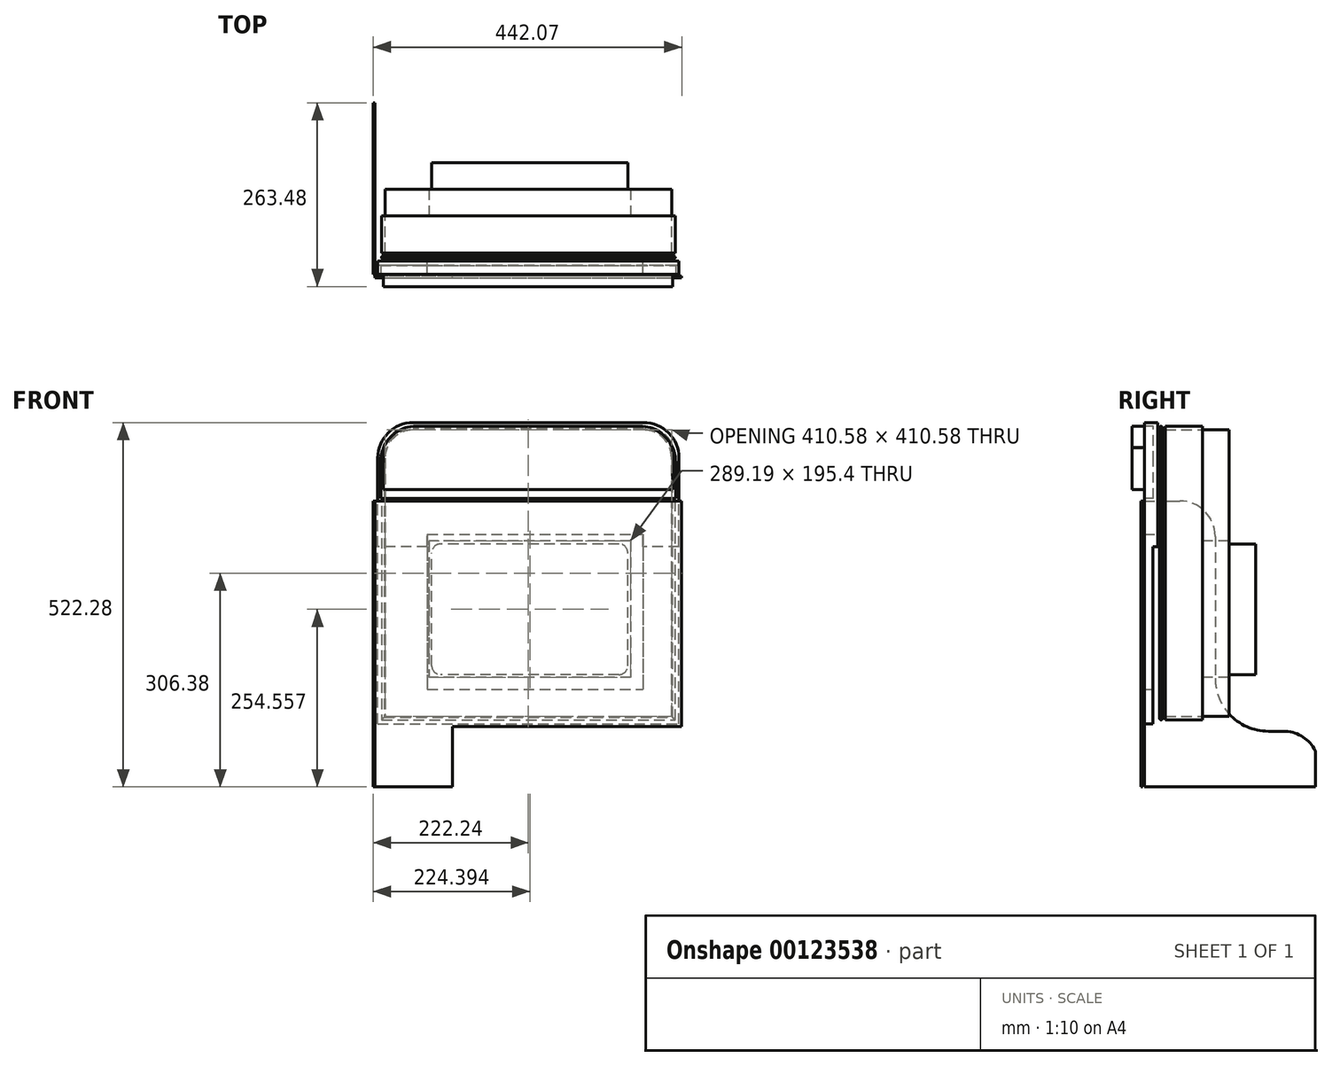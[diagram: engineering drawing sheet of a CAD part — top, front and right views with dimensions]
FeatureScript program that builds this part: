
annotation { "Feature Type Name" : "Feature", "Feature Type Description" : "" }
export const myFeature = defineFeature(function(context is Context, id is Id, definition is map)
    precondition{}
    {
        {
            var Q0;
            Q0=qCreatedBy(makeId("Front.planeOp"),FACE);
            var sketch = newSketch(context, id + "F0", { "sketchPlane" : qUnion([Q0])});
            skLineSegment(sketch, "E0.bottom", {"start": v(0, 0) * mm, "end": v(431.8, 0) * mm});
            skLineSegment(sketch, "E0.top", {"start": v(50.8, 431.8) * mm, "end": v(381, 431.8) * mm});
            skLineSegment(sketch, "E0.left", {"start": v(0, 0) * mm, "end": v(0, 381) * mm});
            skLineSegment(sketch, "E0.right", {"start": v(431.8, 0) * mm, "end": v(431.8, 381) * mm});
            skPoint(sketch, "E1.visualSharp", {"position": v(0, 431.8) * mm});
            skArc(sketch, "E1.filletArc", {"start": v(50.8, 431.8) * mm, "mid": v(14.88, 416.92) * mm, "end": v(0, 381) * mm});
            skPoint(sketch, "E2.visualSharp", {"position": v(431.8, 431.8) * mm});
            skArc(sketch, "E2.filletArc", {"start": v(431.8, 381) * mm, "mid": v(416.92, 416.92) * mm, "end": v(381, 431.8) * mm});
            skSolve(sketch);
        }
        {
            var Q0;
            Q0 = qSketchRegion(id + "F0", true);
            extrude(context, id + "F1", {"entities" : qUnion([Q0]), "depth" : 19.05 * mm});
        }
        {
            var Q0;
            Q0=makeQuery(id+"F1.opExtrude","SWEPT_FACE",FACE,{"disambiguationData":[OSD([sQuery(id+"F0.wireOp",EDGE,"E0.left")])]});
            var sketch = newSketch(context, id + "F2", { "sketchPlane" : qUnion([Q0])});
            skLineSegment(sketch, "E3.bottom", {"start": v(0, 0) * mm, "end": v(6.8, 0) * mm});
            skLineSegment(sketch, "E3.top", {"start": v(0, 254) * mm, "end": v(6.8, 254) * mm});
            skLineSegment(sketch, "E3.left", {"start": v(0, 0) * mm, "end": v(0, 254) * mm});
            skLineSegment(sketch, "E3.right", {"start": v(6.8, 0) * mm, "end": v(6.8, 254) * mm});
            skSolve(sketch);
        }
        {
            var Q0;
            Q0=makeQuery(id+"F2.imprint","IMPRINT",FACE,{"disambiguationData":[TD([[makeQuery(id+"F2.imprint","IMPRINT",EDGE,{"derivedFrom":sQuery(id+"F2.wireOp",EDGE,"E3.bottom")}),-1.0]])]});
            extrude(context, id + "F3", {"entities" : qUnion([Q0]), "operationType" : NewBodyOperationType.REMOVE, "oppositeDirection" : true, "depth" : 431.8 * mm});
        }
        {
            var Q0;
            Q0=makeQuery(id+"F0.imprint","IMPRINT",FACE,{"disambiguationData":[TD([[makeQuery(id+"F0.imprint","IMPRINT",EDGE,{"derivedFrom":sQuery(id+"F0.wireOp",EDGE,"E0.bottom")}),1.0]])]});
            var sketch = newSketch(context, id + "F4", { "sketchPlane" : qUnion([Q0])});
            skLineSegment(sketch, "E4.bottom", {"start": v(380.1, 49.43) * mm, "end": v(71.18, 49.43) * mm});
            skLineSegment(sketch, "E4.top", {"start": v(380.1, 271.62) * mm, "end": v(71.18, 271.62) * mm});
            skLineSegment(sketch, "E4.left", {"start": v(380.1, 49.43) * mm, "end": v(380.1, 271.62) * mm});
            skLineSegment(sketch, "E4.right", {"start": v(71.18, 49.43) * mm, "end": v(71.18, 271.62) * mm});
            skSolve(sketch);
        }
        {
            var Q0;
            Q0 = qSketchRegion(id + "F4", true);
            extrude(context, id + "F5", {"entities" : qUnion([Q0]), "operationType" : NewBodyOperationType.REMOVE, "depth" : 25.4 * mm});
        }
        {
            var Q0;
            Q0=qCreatedBy(makeId("Right.planeOp"),FACE);
            var sketch = newSketch(context, id + "F6", { "sketchPlane" : qUnion([Q0])});
            skCircle(sketch, "E5", {"center": v(4.9, 7.38) * mm, "radius": 1.9 * mm});
            skSolve(sketch);
        }
        {
            var Q0;
            Q0=makeQuery(id+"F6.imprint","IMPRINT",FACE,{"disambiguationData":[TD([[makeQuery(id+"F6.imprint","IMPRINT",EDGE,{"derivedFrom":sQuery(id+"F6.wireOp",EDGE,"E5")}),1.0]])]});
            var Q1;
            Q1=sQuery(id+"F0.wireOp",EDGE,"E0.right");
            var Q2;
            Q2=sQuery(id+"F0.wireOp",EDGE,"E2.filletArc");
            var Q3;
            Q3=sQuery(id+"F0.wireOp",EDGE,"E0.top");
            var Q4;
            Q4=sQuery(id+"F0.wireOp",EDGE,"E1.filletArc");
            var Q5;
            Q5=sQuery(id+"F0.wireOp",EDGE,"E0.left");
            var Q6;
            Q6=sQuery(id+"F0.wireOp",EDGE,"E0.bottom");
            sweep(context, id + "F7", {"profiles" : qUnion([Q0]), "path" : qUnion([Q1, Q2, Q3, Q4, Q5, Q6])});
        }
        {
            var Q0;
            Q0=qCreatedBy(makeId("Right.planeOp"),FACE);
            var sketch = newSketch(context, id + "F8", { "sketchPlane" : qUnion([Q0])});
            skLineSegment(sketch, "E6.bottom", {"start": v(11.24, 5.26) * mm, "end": v(64.2, 5.26) * mm});
            skLineSegment(sketch, "E6.top", {"start": v(11.24, 10.61) * mm, "end": v(64.2, 10.61) * mm});
            skLineSegment(sketch, "E6.left", {"start": v(11.24, 5.26) * mm, "end": v(11.24, 10.61) * mm});
            skLineSegment(sketch, "E6.right", {"start": v(64.2, 5.26) * mm, "end": v(64.2, 10.61) * mm});
            skSolve(sketch);
        }
        {
            var Q0;
            Q0=makeQuery(id+"F8.imprint","IMPRINT",FACE,{"disambiguationData":[TD([[makeQuery(id+"F8.imprint","IMPRINT",EDGE,{"derivedFrom":sQuery(id+"F8.wireOp",EDGE,"E6.bottom")}),1.0]])]});
            var Q1;
            Q1=makeQuery(id+"F1.opExtrude","CAP_EDGE",EDGE,{"disambiguationData":[OSD([sQuery(id+"F0.wireOp",EDGE,"E0.left")])],"isStart":false});
            var Q2;
            Q2=makeQuery(id+"F1.opExtrude","CAP_EDGE",EDGE,{"disambiguationData":[OSD([sQuery(id+"F0.wireOp",EDGE,"E1.filletArc")])],"isStart":false});
            var Q3;
            Q3=makeQuery(id+"F1.opExtrude","CAP_EDGE",EDGE,{"disambiguationData":[OSD([sQuery(id+"F0.wireOp",EDGE,"E0.top")])],"isStart":false});
            var Q4;
            Q4=makeQuery(id+"F1.opExtrude","CAP_EDGE",EDGE,{"disambiguationData":[OSD([sQuery(id+"F0.wireOp",EDGE,"E2.filletArc")])],"isStart":false});
            var Q5;
            Q5=makeQuery(id+"F1.opExtrude","CAP_EDGE",EDGE,{"disambiguationData":[OSD([sQuery(id+"F0.wireOp",EDGE,"E0.right")])],"isStart":false});
            var Q6;
            Q6=makeQuery(id+"F1.opExtrude","CAP_EDGE",EDGE,{"disambiguationData":[OSD([sQuery(id+"F0.wireOp",EDGE,"E0.bottom")])],"isStart":false});
            sweep(context, id + "F9", {"profiles" : qUnion([Q0]), "path" : qUnion([Q1, Q2, Q3, Q4, Q5, Q6])});
        }
        {
            var Q0;
            Q0=makeQuery(id+"F1.opExtrude","CAP_FACE",FACE,{"disambiguationData":[OSD([sQuery(id+"F0.wireOp",EDGE,"E0.bottom"),sQuery(id+"F0.wireOp",EDGE,"E0.top"),sQuery(id+"F0.wireOp",EDGE,"E0.left"),sQuery(id+"F0.wireOp",EDGE,"E0.right"),sQuery(id+"F0.wireOp",EDGE,"E1.filletArc"),sQuery(id+"F0.wireOp",EDGE,"E2.filletArc")])],"isStart":false});
            var sketch = newSketch(context, id + "F10", { "sketchPlane" : qUnion([Q0])});
            skLineSegment(sketch, "E7.bottom", {"start": v(4.2, 322.79) * mm, "end": v(426.84, 322.79) * mm});
            skLineSegment(sketch, "E7.top", {"start": v(55, 426.58) * mm, "end": v(376.04, 426.58) * mm});
            skLineSegment(sketch, "E7.left", {"start": v(4.2, 322.79) * mm, "end": v(4.2, 375.78) * mm});
            skLineSegment(sketch, "E7.right", {"start": v(426.84, 322.79) * mm, "end": v(426.84, 375.78) * mm});
            skPoint(sketch, "E8.visualSharp", {"position": v(4.2, 426.58) * mm});
            skArc(sketch, "E8.filletArc", {"start": v(55, 426.58) * mm, "mid": v(19.07, 411.7) * mm, "end": v(4.2, 375.78) * mm});
            skPoint(sketch, "E9.visualSharp", {"position": v(426.84, 426.58) * mm});
            skArc(sketch, "E9.filletArc", {"start": v(426.84, 375.78) * mm, "mid": v(411.97, 411.7) * mm, "end": v(376.04, 426.58) * mm});
            skSolve(sketch);
        }
        {
            var Q0;
            Q0=makeQuery(id+"F10.imprint","IMPRINT",FACE,{"disambiguationData":[TD([[makeQuery(id+"F10.imprint","IMPRINT",EDGE,{"derivedFrom":sQuery(id+"F10.wireOp",EDGE,"E7.bottom")}),1.0]])]});
            extrude(context, id + "F11", {"entities" : qUnion([Q0]), "operationType" : NewBodyOperationType.REMOVE, "oppositeDirection" : true, "depth" : 12.7 * mm});
        }
        {
            var Q0;
            Q0=makeQuery(id+"F1.opExtrude","CAP_FACE",FACE,{"disambiguationData":[OSD([sQuery(id+"F0.wireOp",EDGE,"E0.bottom"),sQuery(id+"F0.wireOp",EDGE,"E0.top"),sQuery(id+"F0.wireOp",EDGE,"E0.left"),sQuery(id+"F0.wireOp",EDGE,"E0.right"),sQuery(id+"F0.wireOp",EDGE,"E1.filletArc"),sQuery(id+"F0.wireOp",EDGE,"E2.filletArc")])],"isStart":false});
            var sketch = newSketch(context, id + "F12", { "sketchPlane" : qUnion([Q0])});
            skLineSegment(sketch, "E10.bottom", {"start": v(7.94, 335.82) * mm, "end": v(422.56, 335.82) * mm});
            skLineSegment(sketch, "E10.top", {"start": v(58.74, 450.12) * mm, "end": v(371.76, 450.12) * mm});
            skLineSegment(sketch, "E10.left", {"start": v(7.94, 335.82) * mm, "end": v(7.94, 399.32) * mm});
            skLineSegment(sketch, "E10.right", {"start": v(422.56, 335.82) * mm, "end": v(422.56, 399.32) * mm});
            skPoint(sketch, "E11.visualSharp", {"position": v(7.94, 450.12) * mm});
            skArc(sketch, "E11.filletArc", {"start": v(58.74, 450.12) * mm, "mid": v(22.81, 435.24) * mm, "end": v(7.94, 399.32) * mm});
            skPoint(sketch, "E12.visualSharp", {"position": v(422.56, 450.12) * mm});
            skArc(sketch, "E12.filletArc", {"start": v(422.56, 399.32) * mm, "mid": v(407.69, 435.24) * mm, "end": v(371.76, 450.12) * mm});
            skSolve(sketch);
        }
        {
            var Q0;
            {var subQ2=sQuery(id+"F12.wireOp",EDGE,"E10.bottom");Q0=makeQuery(id+"F12.imprint","IMPRINT",FACE,{"disambiguationData":[TD([[makeQuery(id+"F12.imprint","IMPRINT",EDGE,{"derivedFrom":subQ2}),1.0]])]});}
            extrude(context, id + "F13", {"entities" : qUnion([Q0]), "depth" : 17.78 * mm});
        }
        {
            var Q0;
            Q0=makeQuery(id+"F9.opSweep","SWEPT_FACE",FACE,{"disambiguationData":[OSD([sQuery(id+"F0.wireOp",EDGE,"E0.bottom"),sQuery(id+"F8.wireOp",EDGE,"E6.right")])]});
            var sketch = newSketch(context, id + "F14", { "sketchPlane" : qUnion([Q0])});
            skLineSegment(sketch, "E13.bottom", {"start": v(-432.22, 0) * mm, "end": v(0, 0) * mm});
            skLineSegment(sketch, "E13.top", {"start": v(-381.42, 432.66) * mm, "end": v(-50.8, 432.66) * mm});
            skLineSegment(sketch, "E13.left", {"start": v(-432.22, 0) * mm, "end": v(-432.22, 381.86) * mm});
            skLineSegment(sketch, "E13.right", {"start": v(0, 0) * mm, "end": v(0, 381.86) * mm});
            skPoint(sketch, "E14.visualSharp", {"position": v(-432.22, 432.66) * mm});
            skArc(sketch, "E14.filletArc", {"start": v(-425.87, 432.66) * mm, "mid": v(-430.36, 430.8) * mm, "end": v(-432.22, 426.3) * mm});
            skPoint(sketch, "E15.visualSharp", {"position": v(0, 432.66) * mm});
            skArc(sketch, "E15.filletArc", {"start": v(0, 381.86) * mm, "mid": v(-14.88, 417.78) * mm, "end": v(-50.8, 432.66) * mm});
            skArc(sketch, "E16.filletArc", {"start": v(-381.42, 432.66) * mm, "mid": v(-417.34, 417.78) * mm, "end": v(-432.22, 381.86) * mm});
            skLineSegment(sketch, "E17.bottom", {"start": v(-362.65, 261.78) * mm, "end": v(-73.46, 261.78) * mm});
            skLineSegment(sketch, "E17.top", {"start": v(-362.65, 66.38) * mm, "end": v(-73.46, 66.38) * mm});
            skLineSegment(sketch, "E17.left", {"start": v(-362.65, 261.78) * mm, "end": v(-362.65, 66.38) * mm});
            skLineSegment(sketch, "E17.right", {"start": v(-73.46, 261.78) * mm, "end": v(-73.46, 66.38) * mm});
            skSolve(sketch);
        }
        {
            var Q0;
            Q0=makeQuery(id+"F14.imprint","IMPRINT",FACE,{"disambiguationData":[TD([[makeQuery(id+"F14.imprint","IMPRINT",EDGE,{"derivedFrom":sQuery(id+"F14.wireOp",EDGE,"E17.bottom")}),1.0]])]});
            extrude(context, id + "F15", {"entities" : qUnion([Q0]), "depth" : 38.1 * mm});
        }
        {
            var Q0;
            Q0=makeQuery(id+"F15.opExtrude","CAP_FACE",FACE,{"disambiguationData":[OSD([sQuery(id+"F0.wireOp",EDGE,"E0.bottom"),sQuery(id+"F0.wireOp",EDGE,"E0.top"),sQuery(id+"F0.wireOp",EDGE,"E0.left"),sQuery(id+"F0.wireOp",EDGE,"E0.right"),sQuery(id+"F0.wireOp",EDGE,"E1.filletArc"),sQuery(id+"F0.wireOp",EDGE,"E2.filletArc"),sQuery(id+"F8.wireOp",EDGE,"E6.top"),sQuery(id+"F8.wireOp",EDGE,"E6.right"),sQuery(id+"F14.wireOp",EDGE,"E17.bottom"),sQuery(id+"F14.wireOp",EDGE,"E17.top"),sQuery(id+"F14.wireOp",EDGE,"E17.left"),sQuery(id+"F14.wireOp",EDGE,"E17.right")])],"isStart":false});
            var sketch = newSketch(context, id + "F16", { "sketchPlane" : qUnion([Q0])});
            skLineSegment(sketch, "E18.bottom", {"start": v(-345.82, 70.33) * mm, "end": v(-90.05, 70.33) * mm});
            skLineSegment(sketch, "E18.top", {"start": v(-345.82, 257.63) * mm, "end": v(-90.05, 257.63) * mm});
            skLineSegment(sketch, "E18.left", {"start": v(-358.52, 83.03) * mm, "end": v(-358.52, 244.93) * mm});
            skLineSegment(sketch, "E18.right", {"start": v(-77.35, 83.03) * mm, "end": v(-77.35, 244.93) * mm});
            skPoint(sketch, "E19.visualSharp", {"position": v(-358.52, 257.63) * mm});
            skArc(sketch, "E19.filletArc", {"start": v(-345.82, 257.63) * mm, "mid": v(-354.8, 253.91) * mm, "end": v(-358.52, 244.93) * mm});
            skPoint(sketch, "E20.visualSharp", {"position": v(-77.35, 257.63) * mm});
            skArc(sketch, "E20.filletArc", {"start": v(-77.35, 244.93) * mm, "mid": v(-81.07, 253.91) * mm, "end": v(-90.05, 257.63) * mm});
            skPoint(sketch, "E21.visualSharp", {"position": v(-77.35, 70.33) * mm});
            skArc(sketch, "E21.filletArc", {"start": v(-90.05, 70.33) * mm, "mid": v(-81.07, 74.05) * mm, "end": v(-77.35, 83.03) * mm});
            skPoint(sketch, "E22.visualSharp", {"position": v(-358.52, 70.33) * mm});
            skArc(sketch, "E22.filletArc", {"start": v(-358.52, 83.03) * mm, "mid": v(-354.8, 74.05) * mm, "end": v(-345.82, 70.33) * mm});
            skSolve(sketch);
        }
        {
            var Q0;
            Q0=makeQuery(id+"F16.imprint","IMPRINT",FACE,{"disambiguationData":[TD([[makeQuery(id+"F16.imprint","IMPRINT",EDGE,{"derivedFrom":sQuery(id+"F16.wireOp",EDGE,"E18.bottom")}),1.0]])]});
            extrude(context, id + "F17", {"entities" : qUnion([Q0]), "depth" : 38.1 * mm});
        }
        {
            var Q0;
            Q0=makeQuery(id+"F1.opExtrude","CAP_FACE",FACE,{"disambiguationData":[OSD([sQuery(id+"F0.wireOp",EDGE,"E0.bottom"),sQuery(id+"F0.wireOp",EDGE,"E0.top"),sQuery(id+"F0.wireOp",EDGE,"E0.left"),sQuery(id+"F0.wireOp",EDGE,"E0.right"),sQuery(id+"F0.wireOp",EDGE,"E1.filletArc"),sQuery(id+"F0.wireOp",EDGE,"E2.filletArc")])],"isStart":false});
            var sketch = newSketch(context, id + "F18", { "sketchPlane" : qUnion([Q0])});
            skLineSegment(sketch, "E23.top", {"start": v(-3.8, 319.48) * mm, "end": v(435.73, 319.48) * mm});
            skLineSegment(sketch, "E23.left", {"start": v(-3.8, -3.8) * mm, "end": v(-3.8, 319.48) * mm});
            skLineSegment(sketch, "E23.right", {"start": v(435.73, -3.8) * mm, "end": v(435.73, 319.48) * mm});
            skLineSegment(sketch, "E24.top", {"start": v(-3.8, -90.48) * mm, "end": v(106.9, -90.48) * mm});
            skLineSegment(sketch, "E24.left", {"start": v(-3.8, -3.8) * mm, "end": v(-3.8, -90.48) * mm});
            skLineSegment(sketch, "E24.right", {"start": v(106.9, -3.8) * mm, "end": v(106.9, -90.48) * mm});
            skLineSegment(sketch, "E25", {"start": v(106.9, -3.8) * mm, "end": v(435.73, -3.8) * mm});
            skSolve(sketch);
        }
        {
            var Q0;
            Q0 = qSketchRegion(id + "F18", true);
            extrude(context, id + "F19", {"entities" : qUnion([Q0]), "operationType" : NewBodyOperationType.ADD, "depth" : 5.08 * mm});
        }
        {
            var Q0;
            Q0=makeQuery(id+"F19.opExtrude","SWEPT_FACE",FACE,{"disambiguationData":[OSD([sQuery(id+"F18.wireOp",EDGE,"E23.left"),sQuery(id+"F18.wireOp",EDGE,"E24.left")])]});
            var sketch = newSketch(context, id + "F20", { "sketchPlane" : qUnion([Q0])});
            skLineSegment(sketch, "E26", {"start": v(19.05, 319.48) * mm, "end": v(-31.75, 319.48) * mm});
            skLineSegment(sketch, "E27", {"start": v(-82.55, 268.68) * mm, "end": v(-82.55, 65.48) * mm});
            skLineSegment(sketch, "E28", {"start": v(4.18, -10.72) * mm, "end": v(-158.75, -10.72) * mm});
            skPoint(sketch, "E29.visualSharp", {"position": v(-82.55, 319.48) * mm});
            skArc(sketch, "E29.filletArc", {"start": v(-31.75, 319.48) * mm, "mid": v(-67.67, 304.6) * mm, "end": v(-82.55, 268.68) * mm});
            skPoint(sketch, "E30.visualSharp", {"position": v(-82.55, -10.72) * mm});
            skArc(sketch, "E30.filletArc", {"start": v(-158.75, -10.72) * mm, "mid": v(-104.87, 11.6) * mm, "end": v(-82.55, 65.48) * mm});
            skPoint(sketch, "E31.visualSharp", {"position": v(-209.55, -10.72) * mm});
            skLineSegment(sketch, "E32.bottom", {"start": v(-158.75, -10.72) * mm, "end": v(-209.55, -10.72) * mm});
            skLineSegment(sketch, "E32.top", {"start": v(-158.75, -10.72) * mm, "end": v(-180.62, -10.72) * mm});
            skLineSegment(sketch, "E32.left", {"start": v(-158.75, -10.72) * mm, "end": v(-158.75, -10.72) * mm});
            skLineSegment(sketch, "E32.right", {"start": v(-209.55, -10.72) * mm, "end": v(-209.55, -10.72) * mm});
            skLineSegment(sketch, "E33", {"start": v(-224.31, -35.6) * mm, "end": v(-226.65, -39.53) * mm});
            skLineSegment(sketch, "E34", {"start": v(-226.65, -39.53) * mm, "end": v(-226.65, -90.33) * mm});
            skLineSegment(sketch, "E35", {"start": v(-226.65, -90.33) * mm, "end": v(24.13, -90.48) * mm});
            skArc(sketch, "E36.filletArc", {"start": v(-180.62, -10.72) * mm, "mid": v(-205.76, -17.37) * mm, "end": v(-224.31, -35.6) * mm});
            skSolve(sketch);
        }
        {
            var Q0;
            {var subQ0=sQuery(id+"F20.wireOp",EDGE,"E26");Q0=makeQuery(id+"F20.imprint","IMPRINT",FACE,{"disambiguationData":[TD([[makeQuery(id+"F20.imprint","IMPRINT",EDGE,{"derivedFrom":subQ0}),1.0]])]});}
            extrude(context, id + "F21", {"entities" : qUnion([Q0]), "depth" : 2.54 * mm});
        }
        {
            var Q0;
            Q0=makeQuery(id+"F19.opExtrude","SWEPT_FACE",FACE,{"disambiguationData":[OSD([sQuery(id+"F18.wireOp",EDGE,"E23.left"),sQuery(id+"F18.wireOp",EDGE,"E24.left")])]});
            var sketch = newSketch(context, id + "F22", { "sketchPlane" : qUnion([Q0])});
            skLineSegment(sketch, "E37.bottom", {"start": v(21.59, 319.48) * mm, "end": v(19.05, 319.48) * mm});
            skLineSegment(sketch, "E37.top", {"start": v(21.59, -90.48) * mm, "end": v(19.05, -90.48) * mm});
            skLineSegment(sketch, "E37.left", {"start": v(21.59, 319.48) * mm, "end": v(21.59, -90.48) * mm});
            skLineSegment(sketch, "E37.right", {"start": v(19.05, 319.48) * mm, "end": v(19.05, -90.48) * mm});
            skSolve(sketch);
        }
        {
            var Q0;
            Q0 = qSketchRegion(id + "F22", true);
            extrude(context, id + "F23", {"entities" : qUnion([Q0]), "operationType" : NewBodyOperationType.REMOVE, "oppositeDirection" : true, "depth" : 443.22 * mm});
        }
    });
